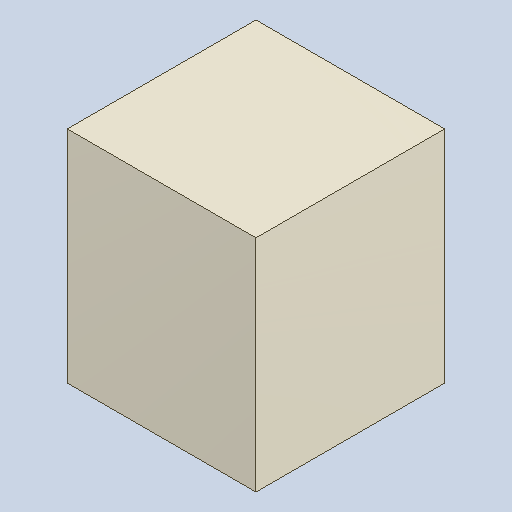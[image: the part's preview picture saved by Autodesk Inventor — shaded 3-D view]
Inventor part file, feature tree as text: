
AUTODESK INVENTOR PART (.ipt)
format: ipt  version: 2023.4 (Build 274418000, 418)  size: 82,944 bytes
history: native  units: mm
features: extrude x1
ambient origin geometry x8: Origin, YZ Plane, XZ Plane, XY Plane, X Axis, Y Axis, Z Axis, Center Point
bodies: Solid1 (feature_tree)
feature tree (1):
  extrude  "Extruded_19"  [1 undecoded]
note: 1 required parameter value undecoded (feature->parameter linkage not recoverable at this tier; creation-order binding heuristic only, values carry confidence <= 0.55)
